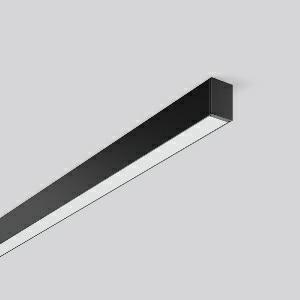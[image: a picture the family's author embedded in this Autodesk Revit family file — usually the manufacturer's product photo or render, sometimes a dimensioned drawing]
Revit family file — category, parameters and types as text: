
# Revit family: less_is_more_27_312197_003_1_76_1d66
name_source: partatom
category: Lighting Fixtures
units: mm (PartAtom-declared; Revit-internal decimal feet)

## family parameters
Cut with Voids When Loaded = No
Host = Face
Light Source = No
Part Type = Normal
Room Calculation Point = No
Round Connector Dimension = Use Diameter
Shared = No

## types (1)
- LESS IS MORE 27 (1 x LED Modul 840, 1800 lm, 4000)
    Apparent Load = 26 VA
    CIE Flux Codes = 65 89 98 100 100
    Color Rendering = 80
    Color Temperature = 4000
    Default Elevation = 1800 mm  [stored 5.90551 ft]
    Description = Series: LESS IS MORE 27
Ceiling luminaire with slim design. Housing: extruded aluminium profile, powder-coated. End cap aluminium powder-coated. Diffuser made of non-yellowing plastic (PMMA) microprismatic. Suitable for Ceiling mounting, Wall (surface). External driver with connecting cable. 
Colour: deep black, matt (RAL 9005)
Length: 1012 mm
Width: 28 mm
Height: 38 mm
Lamp: LED
Socket: without socket
Colour temperature: 4000K
Colour rendering index (CRI): 82
System power: 26 W
Rated luminous flux: 1800 lm
Luminous efficiency: 69 lm/W
Control gear: Voltage converter, DALI dim.
Protection class: II
Type of protection: IP 20
    Height = 38 mm
    Lamp = 1 x LED Modul 840
    Lamp Light Flux = 1800 lm
    Lamp count = 1
    Length = 1012 mm
    Lifetime = 50000 h
    Luminous efficacy = 69 lm/W
    Manufacturer = RZB
    ModVariant = No
    Model = 312197.003.1.76
    Mounting Place = Ceiling, Wall
    Mounting Type = Surface mounted
    Number of Poles = 1
    OnlyDefault = Yes
    Power Factor = 1
    Product Name = LESS IS MORE 27
    Product group = Surface mounted LED linear luminaires
    ProductGroupID = 307
    Protection Class = Protection class II
    Protection Degree = IP 20
    RLX_Detail_Level = 1
    RLX_Emergency_Light_Flux = 0 lm
    RLX_Emergency_Type = 0
    RLX_Emergency_Type_DB = No
    RlxData = <blob elided: 29733 chars, md5=92dc09c7>
    Socket = socket
    Standby Power = 0 W
    System Light Flux = 1800 lm
    System Power = 26 W
    Type Comments = Product without accessories
    Type Image = 312196.003.jpg
    URL = http://relux.com
    VarID = ---
    Voltage = 230 V
    Voltage Range = 220-240 V
    Weight = 0.00 kg
    Width = 28 mm

note: [stored X ft] marks values corroborated as IEEE doubles in the binary element streams (Revit-internal decimal feet)

## geometry (parser evidence)
native form markers: Blend x4, Sweep x8
no freeform markers — native parametric forms only
